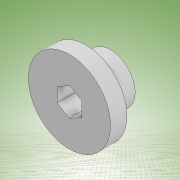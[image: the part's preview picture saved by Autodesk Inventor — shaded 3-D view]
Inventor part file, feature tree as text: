
AUTODESK INVENTOR PART (.ipt)
format: ipt  version: 2022 (Build 260153000, 153)  size: 129,536 bytes
history: native  units: mm
features: extrude x3, sketch x3, other x1
ambient origin geometry x8: Origin, YZ Plane, XZ Plane, XY Plane, X Axis, Y Axis, Z Axis, Center Point
bodies: Body1 (feature_tree)
feature tree (7):
  other  "Sólido1"
  extrude  "Extrusión1"  Depth=6.0mm TaperAngle=0.0deg
  extrude  "Extrusión2"  Depth=4.0mm TaperAngle=0.0deg
  extrude  "Extrusión3"  TaperAngle=0.0deg  [1 undecoded]
  sketch  "Boceto1"  dims[d0=12.0mm d1=6.0mm d2=0.0mm]
  sketch  "Boceto2"  dims[d3=20.0mm d4=4.0mm d5=0.0mm]
  sketch  "Boceto3"  dims[d6=6.0mm d7=0.0mm d8=0.0mm]
note: 1 required parameter value undecoded (feature->parameter linkage not recoverable at this tier; creation-order binding heuristic only, values carry confidence <= 0.55)
